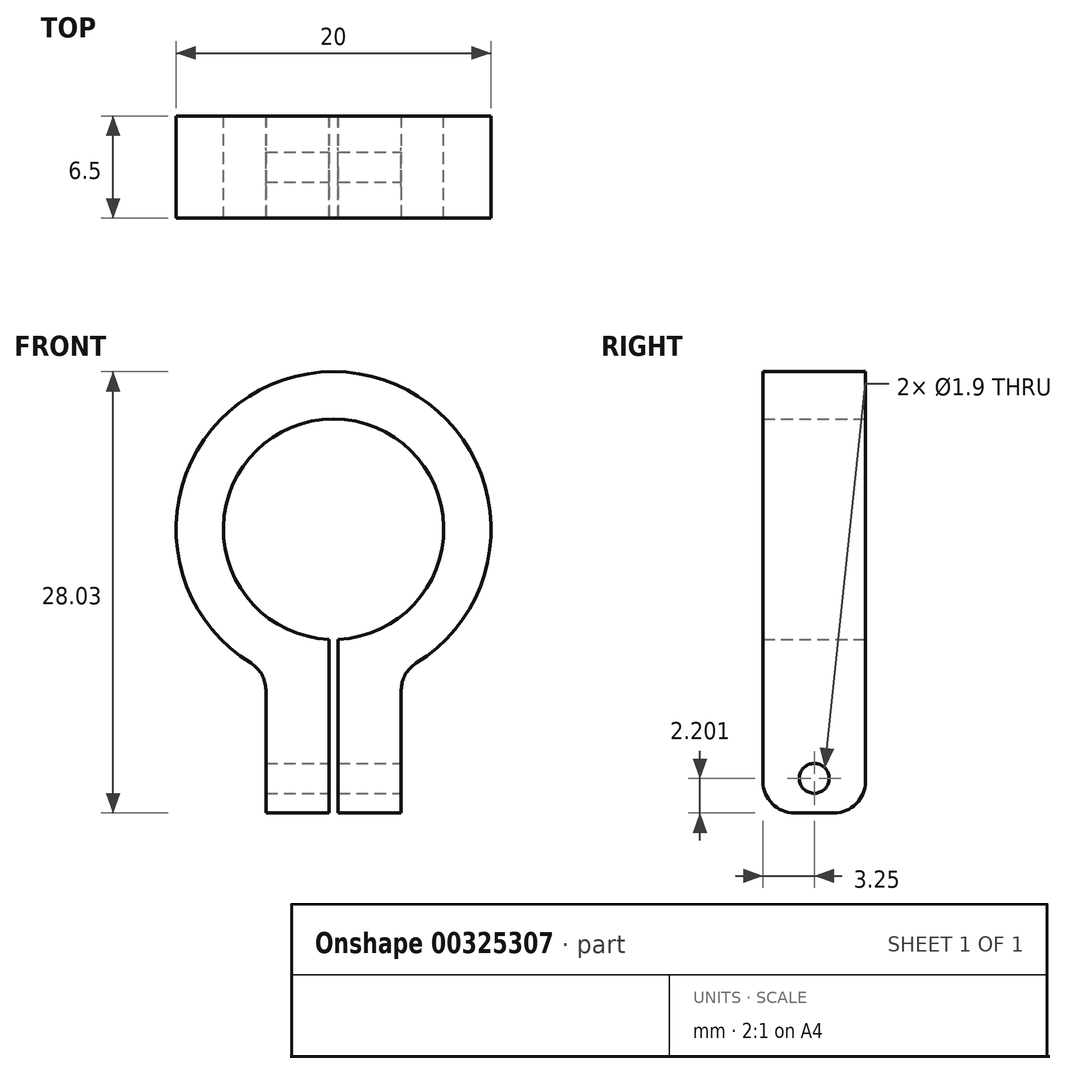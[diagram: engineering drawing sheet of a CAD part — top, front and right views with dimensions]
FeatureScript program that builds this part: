
annotation { "Feature Type Name" : "Feature", "Feature Type Description" : "" }
export const myFeature = defineFeature(function(context is Context, id is Id, definition is map)
    precondition{}
    {
        {
            var Q0;
            Q0=qCreatedBy(makeId("Front.planeOp"),FACE);
            var sketch = newSketch(context, id + "F0", { "sketchPlane" : qUnion([Q0])});
            skArc(sketch, "E0", {"start": v(4.3, -9.03) * mm, "mid": v(0, 10) * mm, "end": v(-4.3, -9.03) * mm});
            skLineSegment(sketch, "E1", {"start": v(-0.3, -18.03) * mm, "end": v(-4.3, -18.03) * mm});
            skLineSegment(sketch, "E2", {"start": v(-4.3, -18.03) * mm, "end": v(-4.3, -9.03) * mm});
            skLineSegment(sketch, "E3.MirrorCS", {"start": v(0.3, -18.03) * mm, "end": v(4.3, -18.03) * mm});
            skLineSegment(sketch, "E4.MirrorCS", {"start": v(4.3, -18.03) * mm, "end": v(4.3, -9.03) * mm});
            skPoint(sketch, "E5.trimOffspring.end.orphan", {"position": v(-4.3, -0.6) * mm});
            skPoint(sketch, "E6.orphan", {"position": v(4.3, -0.6) * mm});
            skArc(sketch, "E7", {"start": v(0.3, -7) * mm, "mid": v(0, 7) * mm, "end": v(-0.3, -7) * mm});
            skLineSegment(sketch, "E8", {"start": v(-0.3, -18.03) * mm, "end": v(-0.3, -7) * mm});
            skLineSegment(sketch, "E9.MirrorCS", {"start": v(0.3, -18.03) * mm, "end": v(0.3, -7) * mm});
            skSolve(sketch);
        }
        {
            var Q0;
            Q0=makeQuery(id+"F0.imprint","IMPRINT",FACE,{"disambiguationData":[TD([[makeQuery(id+"F0.imprint","IMPRINT",EDGE,{"derivedFrom":sQuery(id+"F0.wireOp",EDGE,"E0")}),1.0]])]});
            extrude(context, id + "F1", {"entities" : qUnion([Q0]), "depth" : 6.5 * mm});
        }
        {
            var Q0;
            Q0=makeQuery(id+"F1.opExtrude","SWEPT_FACE",FACE,{"disambiguationData":[OSD([sQuery(id+"F0.wireOp",EDGE,"E4.MirrorCS")])]});
            var sketch = newSketch(context, id + "F2", { "sketchPlane" : qUnion([Q0])});
            skLineSegment(sketch, "E10", {"start": v(-3.25, -9.03) * mm, "end": v(-3.25, -18.03) * mm, "construction": true});
            skCircle(sketch, "E11", {"center": v(-3.25, -15.83) * mm, "radius": 0.95 * mm});
            skSolve(sketch);
        }
        {
            var Q0;
            Q0=makeQuery(id+"F2.imprint","IMPRINT",FACE,{"disambiguationData":[TD([[makeQuery(id+"F2.imprint","IMPRINT",EDGE,{"derivedFrom":sQuery(id+"F2.wireOp",EDGE,"E11")}),1.0]])]});
            extrude(context, id + "F3", {"entities" : qUnion([Q0]), "operationType" : NewBodyOperationType.REMOVE, "oppositeDirection" : true, "depth" : 25 * mm});
        }
        {
            var Q0;
            Q0=makeQuery(id+"F1.opExtrude","CAP_EDGE",EDGE,{"disambiguationData":[OSD([sQuery(id+"F0.wireOp",EDGE,"E3.MirrorCS")])],"isStart":true});
            var Q1;
            Q1=makeQuery(id+"F1.opExtrude","CAP_EDGE",EDGE,{"disambiguationData":[OSD([sQuery(id+"F0.wireOp",EDGE,"E1")])],"isStart":true});
            var Q2;
            Q2=makeQuery(id+"F1.opExtrude","CAP_EDGE",EDGE,{"disambiguationData":[OSD([sQuery(id+"F0.wireOp",EDGE,"E3.MirrorCS")])],"isStart":false});
            var Q3;
            Q3=makeQuery(id+"F1.opExtrude","CAP_EDGE",EDGE,{"disambiguationData":[OSD([sQuery(id+"F0.wireOp",EDGE,"E1")])],"isStart":false});
            fillet(context, id + "F4", {"entities" : qUnion([Q0, Q1, Q2, Q3]), "radius" : 2 * mm, "tangentPropagation" : true, "allowEdgeOverflow" : false});
        }
        {
            var Q0;
            Q0=makeQuery(id+"F1.opExtrude","SWEPT_EDGE",EDGE,{"disambiguationData":[OSD([sQuery(id+"F0.wireOp",EDGE,"E0"),sQuery(id+"F0.wireOp",EDGE,"E4.MirrorCS")])]});
            var Q1;
            Q1=makeQuery(id+"F1.opExtrude","SWEPT_EDGE",EDGE,{"disambiguationData":[OSD([sQuery(id+"F0.wireOp",EDGE,"E0"),sQuery(id+"F0.wireOp",EDGE,"E2")])]});
            fillet(context, id + "F5", {"entities" : qUnion([Q0, Q1]), "radius" : 2 * mm, "tangentPropagation" : true, "allowEdgeOverflow" : false});
        }
    });
